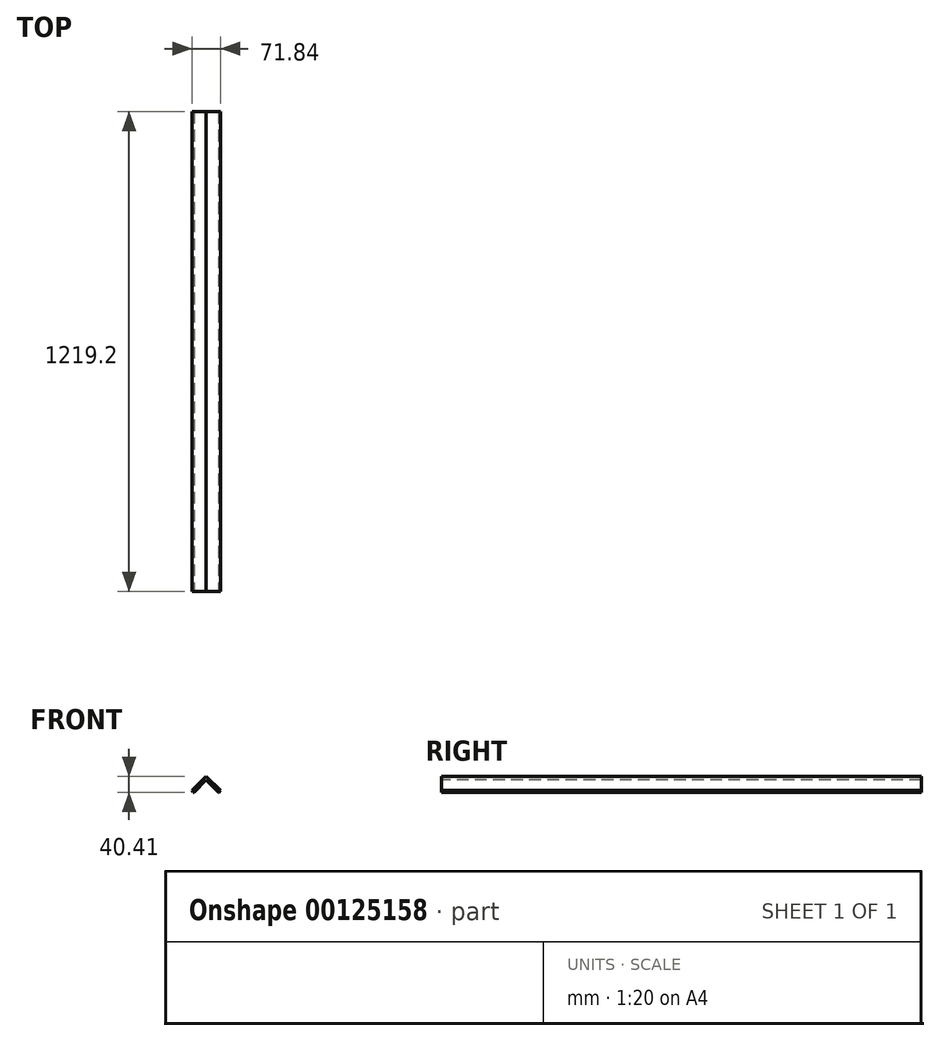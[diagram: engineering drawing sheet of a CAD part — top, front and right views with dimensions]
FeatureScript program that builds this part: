
annotation { "Feature Type Name" : "Feature", "Feature Type Description" : "" }
export const myFeature = defineFeature(function(context is Context, id is Id, definition is map)
    precondition{}
    {
        {
            var Q0;
            Q0=qCreatedBy(makeId("Front.planeOp"),FACE);
            var sketch = newSketch(context, id + "F0", { "sketchPlane" : qUnion([Q0])});
            skLineSegment(sketch, "E0", {"start": v(0, 0) * mm, "end": v(35.92, 35.92) * mm});
            skLineSegment(sketch, "E1", {"start": v(35.92, 35.92) * mm, "end": v(71.84, 0) * mm});
            skLineSegment(sketch, "E2.0", {"start": v(35.92, 26.94) * mm, "end": v(67.35, -4.5) * mm});
            skLineSegment(sketch, "E2.1", {"start": v(4.5, -4.5) * mm, "end": v(35.92, 26.94) * mm});
            skLineSegment(sketch, "E3", {"start": v(4.5, -4.5) * mm, "end": v(2.9, -4.5) * mm});
            skLineSegment(sketch, "E4", {"start": v(67.35, -4.5) * mm, "end": v(68.94, -4.5) * mm});
            skLineSegment(sketch, "E5", {"start": v(2.9, -4.5) * mm, "end": v(0, 0) * mm});
            skLineSegment(sketch, "E6", {"start": v(68.94, -4.5) * mm, "end": v(71.84, 0) * mm});
            skSolve(sketch);
        }
        {
            var Q0;
            Q0=qSketchRegion(id+"F0",true);
            extrude(context, id + "F1", {"entities" : qUnion([Q0]), "oppositeDirection" : true, "depth" : 1219.2 * mm});
        }
    });
